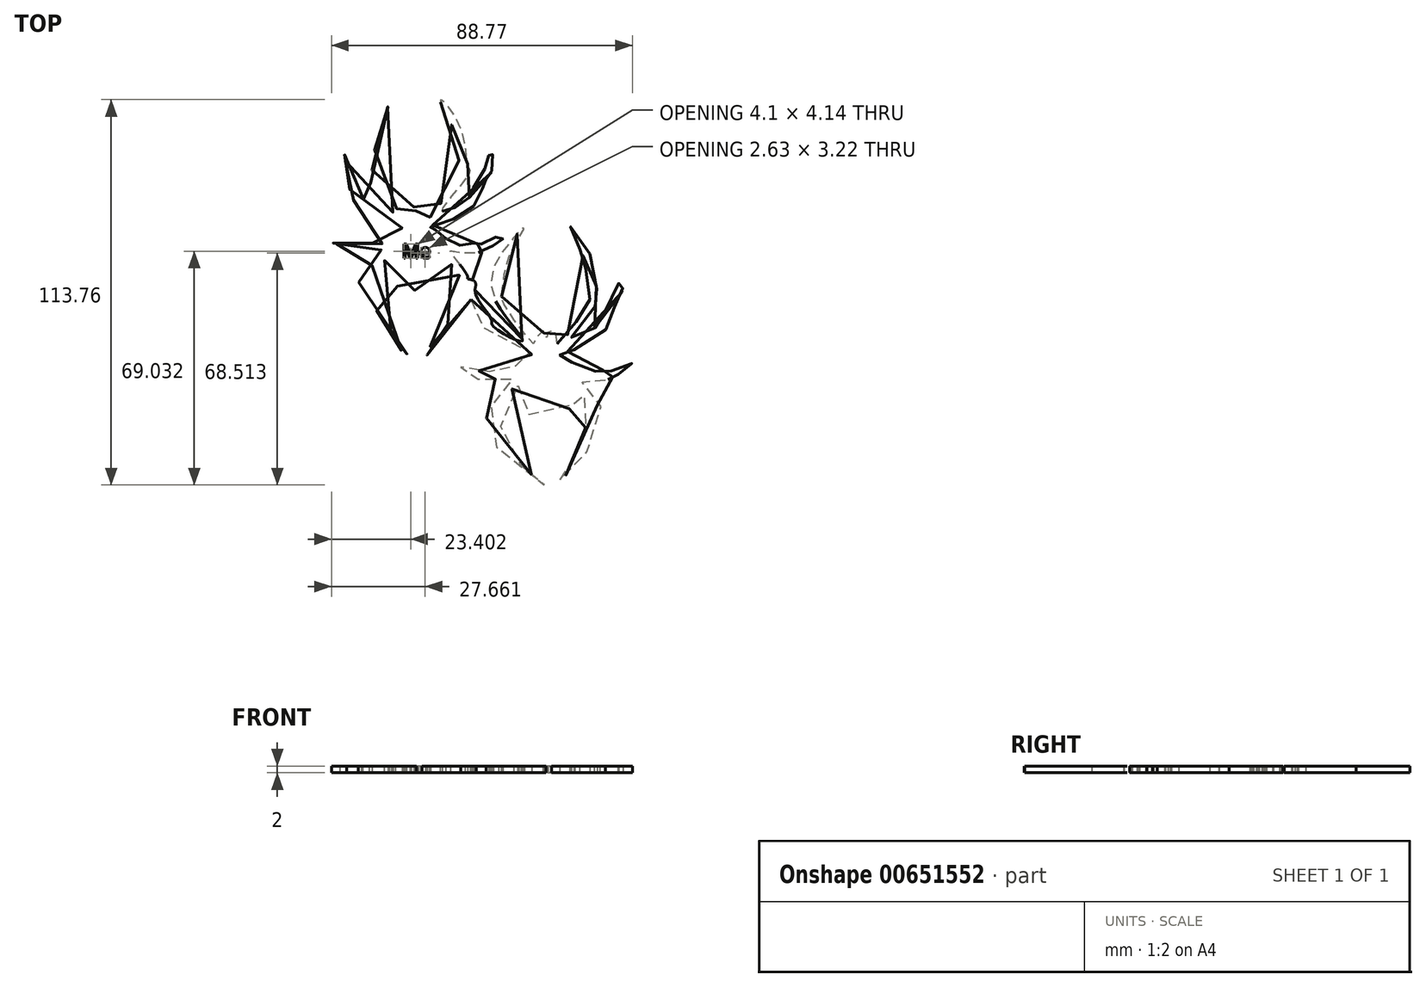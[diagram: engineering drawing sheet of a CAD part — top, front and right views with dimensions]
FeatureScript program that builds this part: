
annotation { "Feature Type Name" : "Feature", "Feature Type Description" : "" }
export const myFeature = defineFeature(function(context is Context, id is Id, definition is map)
    precondition{}
    {
        {
            var Q0;
            Q0=qCreatedBy(makeId("Top.planeOp"),FACE);
            var sketch = newSketch(context, id + "F0", { "sketchPlane" : qUnion([Q0])});
            skFitSpline(sketch, "E0", {"points": [v(-46.14, 29.13) * mm, v(-46.33, 24.48) * mm, v(-39.3, 19.85) * mm, v(-29.67, 24.48) * mm, v(-29.1, 28.92) * mm, v(-23.74, 21.14) * mm, v(-25.03, 19.11) * mm, v(-30.6, 5.4) * mm, v(-32.07, 4.66) * mm, v(-36.33, 0) * mm, v(-27.44, 6.52) * mm, v(-26.89, 7.62) * mm, v(-20.6, 22.07) * mm, v(-22.81, 23.19) * mm, v(-23, 24.1) * mm, v(-28, 31.33) * mm, v(-26.9, 31.33) * mm, v(-18.55, 31.16) * mm, v(-18.37, 31.51) * mm, v(-17.26, 32.26) * mm, v(-12.63, 34.67) * mm, v(-13.18, 35.96) * mm, v(-19.11, 33.37) * mm, v(-20.59, 33.74) * mm, v(-26.7, 33.37) * mm, v(-32.26, 37.63) * mm, v(-33.74, 37.82) * mm, v(-33.74, 38.92) * mm, v(-32.45, 39.11) * mm, v(-20.22, 45.78) * mm, v(-17.8, 52.26) * mm, v(-16.9, 52.63) * mm, v(-15.6, 60.04) * mm, v(-16.7, 60.03) * mm, v(-16.52, 58.93) * mm, v(-21.89, 48.55) * mm, v(-22.44, 47.08) * mm, v(-30.4, 43) * mm, v(-22.26, 54.49) * mm, v(-22.63, 56.15) * mm, v(-25.22, 68.38) * mm, v(-30.96, 76) * mm, v(-26.89, 67.26) * mm, v(-26.52, 65.6) * mm, v(-25.04, 54.67) * mm, v(-25.59, 53.56) * mm, v(-34.11, 41.34) * mm, v(-34.85, 42.26) * mm, v(-35.41, 45.03) * mm, v(-37.44, 45.03) * mm, v(-37.45, 43.56) * mm, v(-38.74, 43.56) * mm, v(-38.56, 45.4) * mm, v(-41.33, 42.44) * mm, v(-41.7, 41.53) * mm, v(-50.78, 53.93) * mm, v(-50.96, 56.15) * mm, v(-48.93, 67.08) * mm, v(-44.3, 76) * mm, v(-50.6, 68.93) * mm, v(-53.19, 54.86) * mm, v(-45.04, 42.26) * mm, v(-53.93, 47.08) * mm, v(-53.93, 48.37) * mm, v(-58.56, 55.78) * mm, v(-59.3, 60.22) * mm, v(-60.03, 60.04) * mm, v(-60.22, 55.04) * mm, v(-57.82, 50.22) * mm, v(-55.97, 45.78) * mm, v(-42.45, 38.74) * mm, v(-42.45, 37.64) * mm, v(-43.74, 38) * mm, v(-48.75, 33.19) * mm, v(-49.85, 33.74) * mm, v(-57.26, 33.37) * mm, v(-62.45, 35.59) * mm, v(-62.81, 33.93) * mm, v(-58.75, 33) * mm, v(-58.19, 31.15) * mm, v(-47.65, 31.7) * mm, v(-49.08, 29.86) * mm, v(-53.49, 23.54) * mm, v(-55.05, 21.98) * mm, v(-48.08, 6.47) * mm, v(-38, 0) * mm, v(-45.01, 5.02) * mm, v(-45.43, 6.92) * mm, v(-51.91, 21.14) * mm, v(-46.14, 29.13) * mm]});
            skText(sketch, "E1", { "text": "Me", "fontName": "OpenSans-Regular.ttf"});
            const initialGuessF0  = {"E1": [-0.04228, 0.02932, 1, 0, 0.00418]};
            skSetInitialGuess(sketch, initialGuessF0);
            skSolve(sketch);
        }
        {
            var Q0;
            Q0=sQuery(id+"F0.wireOp",EDGE,"E0");
            extrude(context, id + "F1", {"bodyType" : ToolBodyType.SURFACE, "surfaceEntities" : qUnion([Q0]), "depth" : 2 * mm, "offsetDistance" : 25 * mm});
        }
        {
            var Q0;
            Q0=qCreatedBy(makeId("Top.planeOp"),FACE);
            var sketch = newSketch(context, id + "F2", { "sketchPlane" : qUnion([Q0])});
            skFitSpline(sketch, "E2", {"points": [v(-7.96, -8.36) * mm, v(-8.14, -12.99) * mm, v(-1.1, -17.62) * mm, v(8.53, -12.99) * mm, v(8.7, -8.18) * mm, v(14.45, -16.32) * mm, v(13.16, -18.36) * mm, v(7.6, -32.06) * mm, v(6.12, -32.8) * mm, v(1.86, -37.47) * mm, v(10.75, -30.95) * mm, v(11.3, -29.84) * mm, v(17.6, -15.4) * mm, v(15.38, -14.28) * mm, v(15.2, -13.36) * mm, v(10.2, -6.13) * mm, v(11.3, -6.13) * mm, v(19.64, -6.32) * mm, v(19.82, -5.95) * mm, v(20.93, -5.2) * mm, v(25.57, -2.8) * mm, v(25, -1.5) * mm, v(19.08, -4.1) * mm, v(17.6, -3.73) * mm, v(11.49, -4.1) * mm, v(5.93, 0.16) * mm, v(4.45, 0.35) * mm, v(4.45, 1.46) * mm, v(5.75, 1.65) * mm, v(17.97, 8.31) * mm, v(20.38, 14.8) * mm, v(21.3, 15.17) * mm, v(22.6, 22.57) * mm, v(21.5, 22.57) * mm, v(21.68, 21.46) * mm, v(16.3, 11.1) * mm, v(15.75, 9.6) * mm, v(7.78, 5.54) * mm, v(15.93, 17.02) * mm, v(15.56, 18.69) * mm, v(12.97, 30.9) * mm, v(7.23, 38.52) * mm, v(11.3, 29.8) * mm, v(11.67, 28.13) * mm, v(13.16, 17.2) * mm, v(12.6, 16.1) * mm, v(4.08, 3.87) * mm, v(3.34, 4.8) * mm, v(2.78, 7.57) * mm, v(0.75, 7.57) * mm, v(0.75, 6.1) * mm, v(-0.55, 6.1) * mm, v(-0.36, 7.94) * mm, v(-3.14, 4.98) * mm, v(-3.51, 4.05) * mm, v(-12.59, 16.46) * mm, v(-12.77, 18.69) * mm, v(-10.74, 29.61) * mm, v(-6.1, 38.52) * mm, v(-12.4, 31.46) * mm, v(-15, 17.39) * mm, v(-6.85, 4.8) * mm, v(-15.74, 9.6) * mm, v(-15.74, 10.9) * mm, v(-20.37, 18.31) * mm, v(-21.1, 22.76) * mm, v(-21.85, 22.57) * mm, v(-22.03, 17.57) * mm, v(-19.63, 12.76) * mm, v(-17.77, 8.31) * mm, v(-4.25, 1.28) * mm, v(-4.25, 0.16) * mm, v(-5.55, 0.53) * mm, v(-10.55, -4.28) * mm, v(-11.66, -3.73) * mm, v(-19.07, -4.1) * mm, v(-24.26, -1.87) * mm, v(-24.63, -3.54) * mm, v(-20.55, -4.47) * mm, v(-20, -6.32) * mm, v(-9.44, -5.76) * mm, v(-10.92, -7.61) * mm, v(-15.18, -13.91) * mm, v(-17.22, -15.58) * mm, v(-10.37, -31.7) * mm, v(0.2, -37.47) * mm, v(-6.85, -32.43) * mm, v(-7.22, -30.58) * mm, v(-13.7, -16.32) * mm, v(-7.96, -8.36) * mm]});
            skSolve(sketch);
        }
        {
            var Q0;
            Q0=makeQuery(id+"F2.imprint","IMPRINT",FACE,{"disambiguationData":[TD([[makeQuery(id+"F2.imprint","IMPRINT",EDGE,{"derivedFrom":sQuery(id+"F2.wireOp",EDGE,"E2")}),1.0]])]});
            extrude(context, id + "F3", {"entities" : qUnion([Q0]), "depth" : 2 * mm, "offsetDistance" : 25 * mm});
        }
        {
            var Q0;
            Q0 = qSketchRegion(id + "F0", true);
            extrude(context, id + "F4", {"entities" : qUnion([Q0]), "operationType" : NewBodyOperationType.ADD, "depth" : 2 * mm, "offsetDistance" : 25 * mm});
        }
    });
